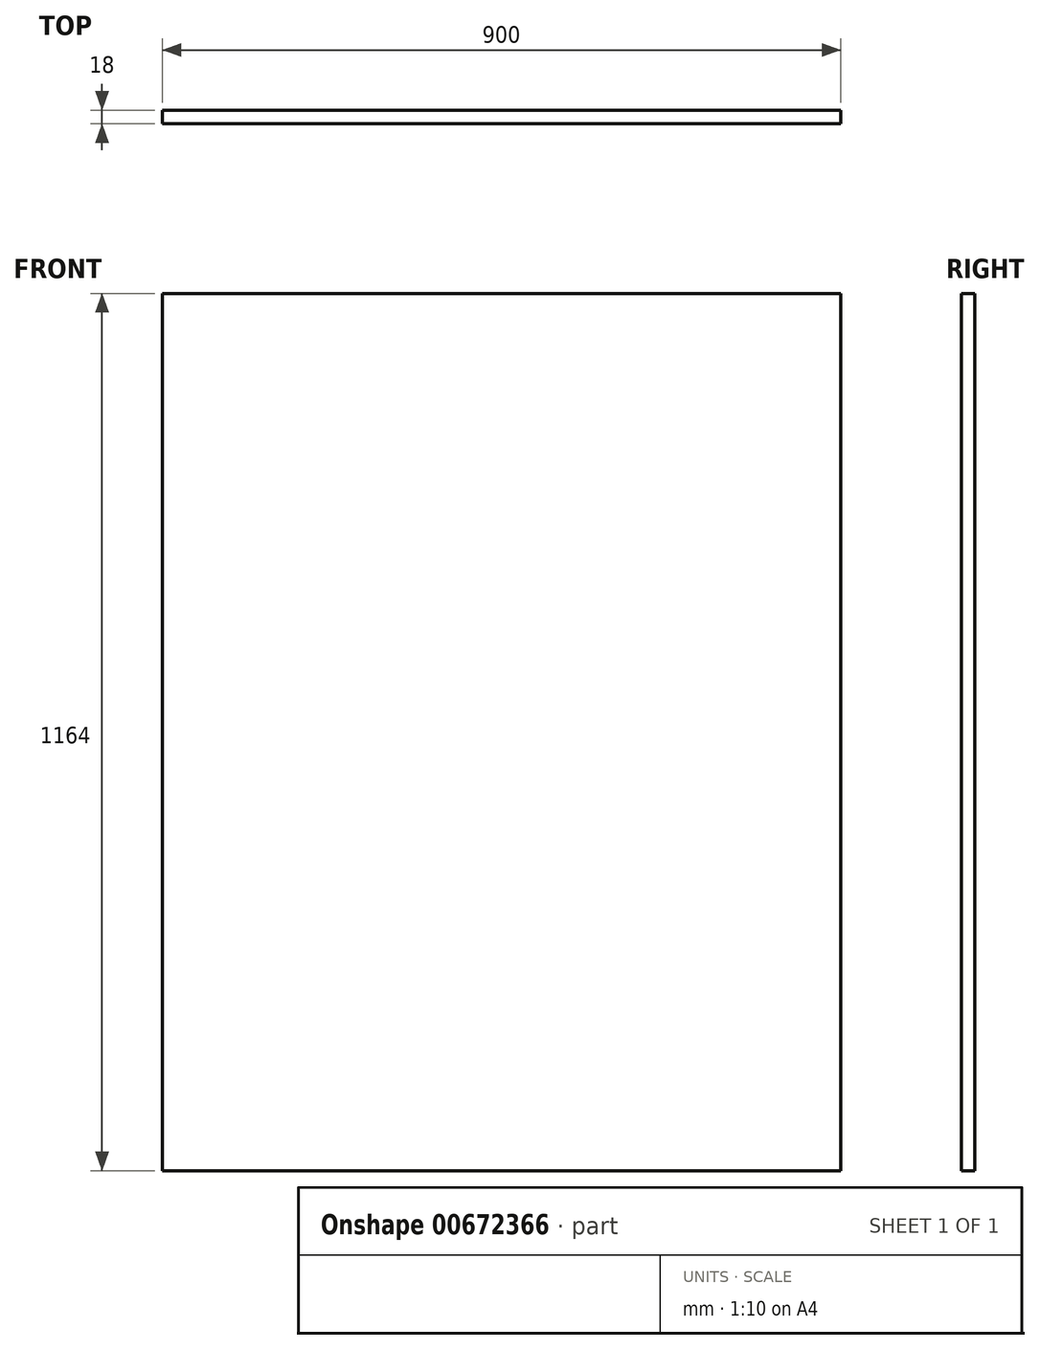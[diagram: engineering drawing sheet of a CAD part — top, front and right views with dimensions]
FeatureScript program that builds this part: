
annotation { "Feature Type Name" : "Feature", "Feature Type Description" : "" }
export const myFeature = defineFeature(function(context is Context, id is Id, definition is map)
    precondition{}
    {
        {
            var Q0;
            Q0=qCreatedBy(makeId("Front.planeOp"),FACE);
            var sketch = newSketch(context, id + "F0", { "sketchPlane" : qUnion([Q0])});
            skLineSegment(sketch, "E0.bottom", {"start": v(0, 0) * mm, "end": v(-900, 0) * mm});
            skLineSegment(sketch, "E0.top", {"start": v(0, 1164) * mm, "end": v(-900, 1164) * mm});
            skLineSegment(sketch, "E0.left", {"start": v(0, 0) * mm, "end": v(0, 1164) * mm});
            skLineSegment(sketch, "E0.right", {"start": v(-900, 0) * mm, "end": v(-900, 1164) * mm});
            skSolve(sketch);
        }
        {
            var Q0;
            Q0=makeQuery(id+"F0.imprint","IMPRINT",FACE,{"disambiguationData":[TD([[makeQuery(id+"F0.imprint","IMPRINT",EDGE,{"derivedFrom":sQuery(id+"F0.wireOp",EDGE,"E0.bottom")}),-1.0]])]});
            extrude(context, id + "F1", {"entities" : qUnion([Q0]), "depth" : 18 * mm, "offsetDistance" : 25 * mm});
        }
    });
